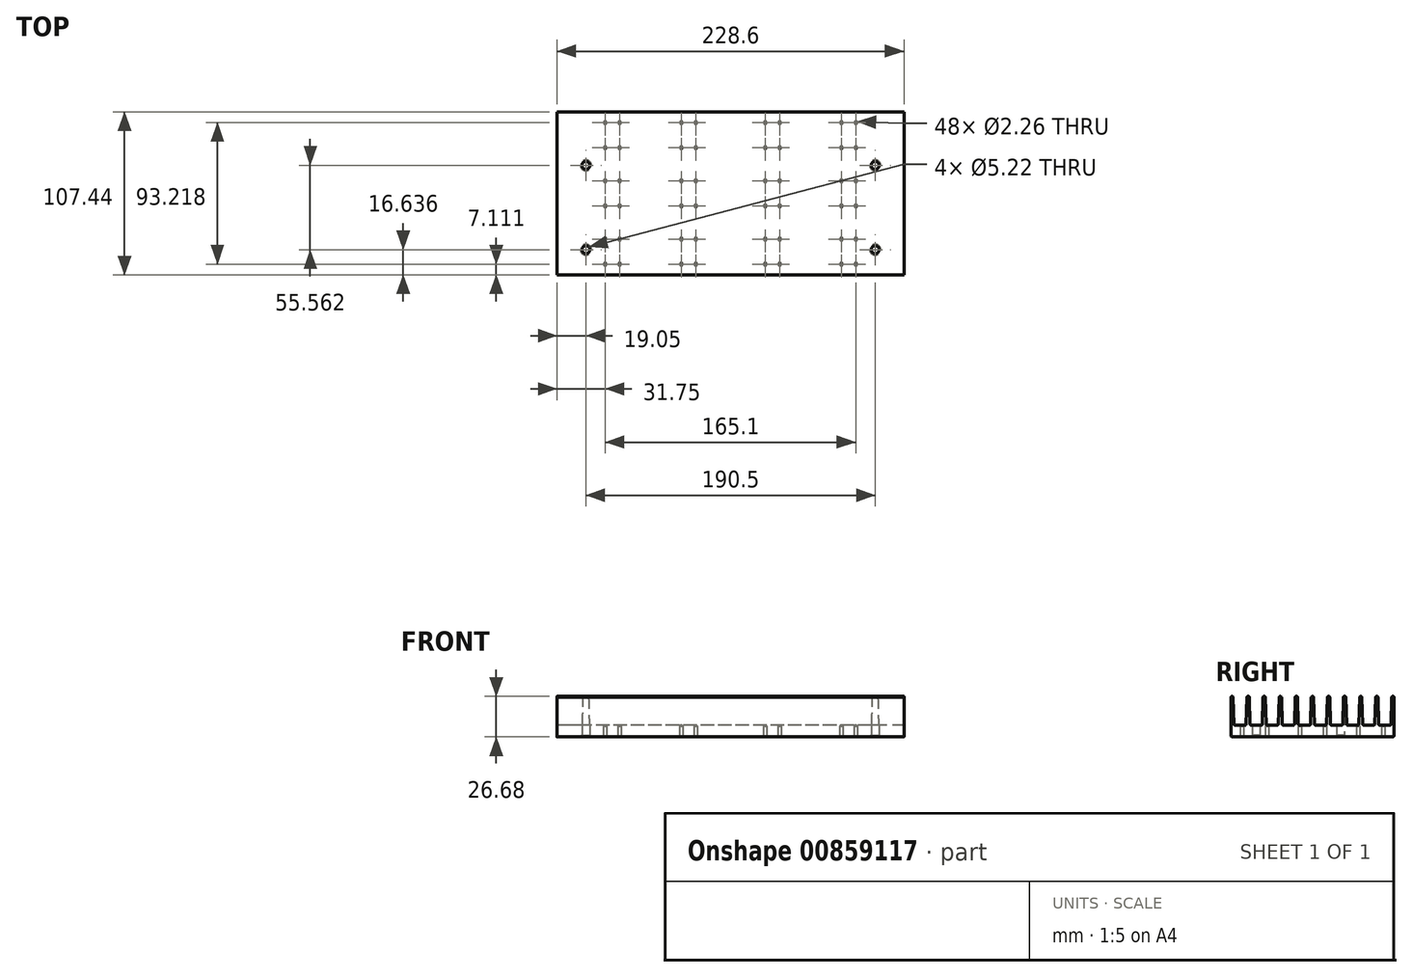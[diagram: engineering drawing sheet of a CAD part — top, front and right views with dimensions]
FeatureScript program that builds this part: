
annotation { "Feature Type Name" : "Feature", "Feature Type Description" : "" }
export const myFeature = defineFeature(function(context is Context, id is Id, definition is map)
    precondition{}
    {
        {
            var Q0;
            Q0=qCreatedBy(makeId("Right.planeOp"),FACE);
            var sketch = newSketch(context, id + "F0", { "sketchPlane" : qUnion([Q0])});
            skLineSegment(sketch, "E0", {"start": v(50.94, -5.71) * mm, "end": v(44.38, -5.71) * mm});
            skArc(sketch, "E1", {"start": v(43.62, -4.97) * mm, "mid": v(43.85, -5.5) * mm, "end": v(44.38, -5.71) * mm});
            skLineSegment(sketch, "E2", {"start": v(43.62, -4.97) * mm, "end": v(43.13, 12.59) * mm});
            skArc(sketch, "E3", {"start": v(43.13, 12.59) * mm, "mid": v(42.37, 13.33) * mm, "end": v(41.6, 12.59) * mm});
            skLineSegment(sketch, "E4", {"start": v(41.6, 12.59) * mm, "end": v(41.11, -4.97) * mm});
            skArc(sketch, "E5", {"start": v(40.35, -5.71) * mm, "mid": v(40.88, -5.5) * mm, "end": v(41.11, -4.97) * mm});
            skLineSegment(sketch, "E6", {"start": v(40.35, -5.71) * mm, "end": v(33.8, -5.71) * mm});
            skArc(sketch, "E7", {"start": v(33.03, -4.97) * mm, "mid": v(33.26, -5.5) * mm, "end": v(33.8, -5.71) * mm});
            skLineSegment(sketch, "E8", {"start": v(33.03, -4.97) * mm, "end": v(32.54, 12.59) * mm});
            skArc(sketch, "E9", {"start": v(32.54, 12.59) * mm, "mid": v(31.78, 13.33) * mm, "end": v(31.01, 12.59) * mm});
            skLineSegment(sketch, "E10", {"start": v(31.01, 12.59) * mm, "end": v(30.52, -4.97) * mm});
            skArc(sketch, "E11", {"start": v(29.76, -5.71) * mm, "mid": v(30.3, -5.5) * mm, "end": v(30.52, -4.97) * mm});
            skLineSegment(sketch, "E12", {"start": v(29.76, -5.71) * mm, "end": v(23.2, -5.71) * mm});
            skArc(sketch, "E13", {"start": v(22.44, -4.97) * mm, "mid": v(22.67, -5.5) * mm, "end": v(23.2, -5.71) * mm});
            skLineSegment(sketch, "E14", {"start": v(22.44, -4.97) * mm, "end": v(21.95, 12.59) * mm});
            skArc(sketch, "E15", {"start": v(21.95, 12.59) * mm, "mid": v(21.18, 13.33) * mm, "end": v(20.42, 12.59) * mm});
            skLineSegment(sketch, "E16", {"start": v(20.42, 12.59) * mm, "end": v(19.93, -4.97) * mm});
            skArc(sketch, "E17", {"start": v(19.17, -5.71) * mm, "mid": v(19.7, -5.5) * mm, "end": v(19.93, -4.97) * mm});
            skLineSegment(sketch, "E18", {"start": v(19.17, -5.71) * mm, "end": v(12.6, -5.71) * mm});
            skArc(sketch, "E19", {"start": v(11.85, -4.97) * mm, "mid": v(12.08, -5.5) * mm, "end": v(12.6, -5.71) * mm});
            skLineSegment(sketch, "E20", {"start": v(11.85, -4.97) * mm, "end": v(11.35, 12.59) * mm});
            skArc(sketch, "E21", {"start": v(11.35, 12.59) * mm, "mid": v(10.6, 13.33) * mm, "end": v(9.83, 12.59) * mm});
            skLineSegment(sketch, "E22", {"start": v(9.83, 12.59) * mm, "end": v(9.34, -4.97) * mm});
            skArc(sketch, "E23", {"start": v(8.58, -5.71) * mm, "mid": v(9.1, -5.5) * mm, "end": v(9.34, -4.97) * mm});
            skLineSegment(sketch, "E24", {"start": v(8.58, -5.71) * mm, "end": v(2.02, -5.71) * mm});
            skArc(sketch, "E25", {"start": v(1.25, -4.97) * mm, "mid": v(1.48, -5.5) * mm, "end": v(2.02, -5.71) * mm});
            skLineSegment(sketch, "E26", {"start": v(1.25, -4.97) * mm, "end": v(0.76, 12.59) * mm});
            skArc(sketch, "E27", {"start": v(0.76, 12.59) * mm, "mid": v(0, 13.33) * mm, "end": v(-0.76, 12.59) * mm});
            skLineSegment(sketch, "E28", {"start": v(-0.76, 12.59) * mm, "end": v(-1.25, -4.97) * mm});
            skArc(sketch, "E29", {"start": v(-2.02, -5.71) * mm, "mid": v(-1.48, -5.5) * mm, "end": v(-1.25, -4.97) * mm});
            skLineSegment(sketch, "E30", {"start": v(-2.02, -5.71) * mm, "end": v(-8.58, -5.71) * mm});
            skArc(sketch, "E31", {"start": v(-9.34, -4.97) * mm, "mid": v(-9.1, -5.5) * mm, "end": v(-8.58, -5.71) * mm});
            skLineSegment(sketch, "E32", {"start": v(-9.34, -4.97) * mm, "end": v(-9.83, 12.59) * mm});
            skArc(sketch, "E33", {"start": v(-9.83, 12.59) * mm, "mid": v(-10.6, 13.33) * mm, "end": v(-11.35, 12.59) * mm});
            skLineSegment(sketch, "E34", {"start": v(-11.35, 12.59) * mm, "end": v(-11.85, -4.97) * mm});
            skArc(sketch, "E35", {"start": v(-12.6, -5.71) * mm, "mid": v(-12.08, -5.5) * mm, "end": v(-11.85, -4.97) * mm});
            skLineSegment(sketch, "E36", {"start": v(-12.6, -5.71) * mm, "end": v(-19.17, -5.71) * mm});
            skArc(sketch, "E37", {"start": v(-19.93, -4.97) * mm, "mid": v(-19.7, -5.5) * mm, "end": v(-19.17, -5.71) * mm});
            skLineSegment(sketch, "E38", {"start": v(-19.93, -4.97) * mm, "end": v(-20.42, 12.59) * mm});
            skArc(sketch, "E39", {"start": v(-20.42, 12.59) * mm, "mid": v(-21.18, 13.34) * mm, "end": v(-21.95, 12.59) * mm});
            skLineSegment(sketch, "E40", {"start": v(-21.95, 12.59) * mm, "end": v(-22.44, -4.97) * mm});
            skArc(sketch, "E41", {"start": v(-23.2, -5.71) * mm, "mid": v(-22.67, -5.5) * mm, "end": v(-22.44, -4.97) * mm});
            skLineSegment(sketch, "E42", {"start": v(-23.2, -5.71) * mm, "end": v(-29.76, -5.71) * mm});
            skArc(sketch, "E43", {"start": v(-30.52, -4.97) * mm, "mid": v(-30.3, -5.5) * mm, "end": v(-29.76, -5.71) * mm});
            skLineSegment(sketch, "E44", {"start": v(-30.52, -4.97) * mm, "end": v(-31.01, 12.59) * mm});
            skArc(sketch, "E45", {"start": v(-31.01, 12.59) * mm, "mid": v(-31.78, 13.33) * mm, "end": v(-32.54, 12.59) * mm});
            skLineSegment(sketch, "E46", {"start": v(-32.54, 12.59) * mm, "end": v(-33.03, -4.97) * mm});
            skArc(sketch, "E47", {"start": v(-33.8, -5.71) * mm, "mid": v(-33.26, -5.5) * mm, "end": v(-33.03, -4.97) * mm});
            skLineSegment(sketch, "E48", {"start": v(-33.8, -5.71) * mm, "end": v(-40.35, -5.71) * mm});
            skArc(sketch, "E49", {"start": v(-41.11, -4.97) * mm, "mid": v(-40.88, -5.5) * mm, "end": v(-40.35, -5.71) * mm});
            skLineSegment(sketch, "E50", {"start": v(-41.11, -4.97) * mm, "end": v(-41.6, 12.59) * mm});
            skArc(sketch, "E51", {"start": v(-41.6, 12.59) * mm, "mid": v(-42.37, 13.33) * mm, "end": v(-43.13, 12.59) * mm});
            skLineSegment(sketch, "E52", {"start": v(-43.13, 12.59) * mm, "end": v(-43.62, -4.97) * mm});
            skArc(sketch, "E53", {"start": v(-44.38, -5.71) * mm, "mid": v(-43.85, -5.5) * mm, "end": v(-43.62, -4.97) * mm});
            skLineSegment(sketch, "E54", {"start": v(-44.38, -5.71) * mm, "end": v(-50.94, -5.71) * mm});
            skArc(sketch, "E55", {"start": v(-51.7, -4.97) * mm, "mid": v(-51.48, -5.5) * mm, "end": v(-50.94, -5.71) * mm});
            skLineSegment(sketch, "E56", {"start": v(-51.7, -4.97) * mm, "end": v(-52.2, 12.59) * mm});
            skArc(sketch, "E57", {"start": v(-52.2, 12.59) * mm, "mid": v(-52.96, 13.34) * mm, "end": v(-53.72, 12.59) * mm});
            skLineSegment(sketch, "E58", {"start": v(-53.72, 12.59) * mm, "end": v(-53.72, -12.57) * mm});
            skArc(sketch, "E59", {"start": v(-53.72, -12.57) * mm, "mid": v(-53.5, -13.11) * mm, "end": v(-52.96, -13.34) * mm});
            skLineSegment(sketch, "E60", {"start": v(-52.96, -13.33) * mm, "end": v(52.96, -13.33) * mm});
            skArc(sketch, "E61", {"start": v(52.96, -13.34) * mm, "mid": v(53.5, -13.11) * mm, "end": v(53.72, -12.57) * mm});
            skLineSegment(sketch, "E62", {"start": v(53.72, -12.57) * mm, "end": v(53.72, 12.59) * mm});
            skArc(sketch, "E63", {"start": v(53.72, 12.59) * mm, "mid": v(52.96, 13.33) * mm, "end": v(52.2, 12.59) * mm});
            skLineSegment(sketch, "E64", {"start": v(52.2, 12.59) * mm, "end": v(51.7, -4.97) * mm});
            skArc(sketch, "E65", {"start": v(50.94, -5.71) * mm, "mid": v(51.48, -5.5) * mm, "end": v(51.7, -4.97) * mm});
            skSolve(sketch);
        }
        {
            var Q0;
            Q0 = qSketchRegion(id + "F0", true);
            extrude(context, id + "F1", {"entities" : qUnion([Q0]), "endBound" : BoundingType.SYMMETRIC, "depth" : 228.6 * mm, "offsetDistance" : 25.4 * mm});
        }
        {
            var Q0;
            Q0=makeQuery(id+"F1.opExtrude","SWEPT_FACE",FACE,{"disambiguationData":[OSD([sQuery(id+"F0.wireOp",EDGE,"E60")])]});
            var sketch = newSketch(context, id + "F2", { "sketchPlane" : qUnion([Q0])});
            skLineSegment(sketch, "E66.0", {"start": v(-114.3, 52.96) * mm, "end": v(-114.3, -52.96) * mm});
            skLineSegment(sketch, "E67.0.2", {"start": v(114.3, -52.96) * mm, "end": v(114.3, 52.96) * mm});
            skPoint(sketch, "E68", {"position": v(-95.25, 37.08) * mm});
            skPoint(sketch, "E69", {"position": v(95.25, 37.08) * mm});
            skPoint(sketch, "E70", {"position": v(14.56, 92.82) * mm});
            skPoint(sketch, "E71", {"position": v(-95.25, -18.48) * mm});
            skPoint(sketch, "E72", {"position": v(95.25, -18.48) * mm});
            skSolve(sketch);
        }
        {
            var Q0;
            Q0=sQuery(id+"F2.wireOp",VERTEX,"E68");
            var Q1;
            Q1=sQuery(id+"F2.wireOp",VERTEX,"E71");
            var Q2;
            Q2=sQuery(id+"F2.wireOp",VERTEX,"E69");
            var Q3;
            Q3=sQuery(id+"F2.wireOp",VERTEX,"E72");
            var Q4;
            Q4=makeQuery(id+"F1.opExtrude","SWEPT_BODY",BODY,{"disambiguationData":[OSD([sQuery(id+"F0.wireOp",EDGE,"E0"),sQuery(id+"F0.wireOp",EDGE,"E1"),sQuery(id+"F0.wireOp",EDGE,"E2"),sQuery(id+"F0.wireOp",EDGE,"E3"),sQuery(id+"F0.wireOp",EDGE,"E4"),sQuery(id+"F0.wireOp",EDGE,"E5"),sQuery(id+"F0.wireOp",EDGE,"E6"),sQuery(id+"F0.wireOp",EDGE,"E7"),sQuery(id+"F0.wireOp",EDGE,"E8"),sQuery(id+"F0.wireOp",EDGE,"E9"),sQuery(id+"F0.wireOp",EDGE,"E10"),sQuery(id+"F0.wireOp",EDGE,"E11"),sQuery(id+"F0.wireOp",EDGE,"E12"),sQuery(id+"F0.wireOp",EDGE,"E13"),sQuery(id+"F0.wireOp",EDGE,"E14"),sQuery(id+"F0.wireOp",EDGE,"E15"),sQuery(id+"F0.wireOp",EDGE,"E16"),sQuery(id+"F0.wireOp",EDGE,"E17"),sQuery(id+"F0.wireOp",EDGE,"E18"),sQuery(id+"F0.wireOp",EDGE,"E19"),sQuery(id+"F0.wireOp",EDGE,"E20"),sQuery(id+"F0.wireOp",EDGE,"E21"),sQuery(id+"F0.wireOp",EDGE,"E22"),sQuery(id+"F0.wireOp",EDGE,"E23"),sQuery(id+"F0.wireOp",EDGE,"E24"),sQuery(id+"F0.wireOp",EDGE,"E25"),sQuery(id+"F0.wireOp",EDGE,"E26"),sQuery(id+"F0.wireOp",EDGE,"E27"),sQuery(id+"F0.wireOp",EDGE,"E28"),sQuery(id+"F0.wireOp",EDGE,"E29"),sQuery(id+"F0.wireOp",EDGE,"E30"),sQuery(id+"F0.wireOp",EDGE,"E31"),sQuery(id+"F0.wireOp",EDGE,"E32"),sQuery(id+"F0.wireOp",EDGE,"E33"),sQuery(id+"F0.wireOp",EDGE,"E34"),sQuery(id+"F0.wireOp",EDGE,"E35"),sQuery(id+"F0.wireOp",EDGE,"E36"),sQuery(id+"F0.wireOp",EDGE,"E37"),sQuery(id+"F0.wireOp",EDGE,"E38"),sQuery(id+"F0.wireOp",EDGE,"E39"),sQuery(id+"F0.wireOp",EDGE,"E40"),sQuery(id+"F0.wireOp",EDGE,"E41"),sQuery(id+"F0.wireOp",EDGE,"E42"),sQuery(id+"F0.wireOp",EDGE,"E43"),sQuery(id+"F0.wireOp",EDGE,"E44"),sQuery(id+"F0.wireOp",EDGE,"E45"),sQuery(id+"F0.wireOp",EDGE,"E46"),sQuery(id+"F0.wireOp",EDGE,"E47"),sQuery(id+"F0.wireOp",EDGE,"E48"),sQuery(id+"F0.wireOp",EDGE,"E49"),sQuery(id+"F0.wireOp",EDGE,"E50"),sQuery(id+"F0.wireOp",EDGE,"E51"),sQuery(id+"F0.wireOp",EDGE,"E52"),sQuery(id+"F0.wireOp",EDGE,"E53"),sQuery(id+"F0.wireOp",EDGE,"E54"),sQuery(id+"F0.wireOp",EDGE,"E55"),sQuery(id+"F0.wireOp",EDGE,"E56"),sQuery(id+"F0.wireOp",EDGE,"E57"),sQuery(id+"F0.wireOp",EDGE,"E58"),sQuery(id+"F0.wireOp",EDGE,"E59"),sQuery(id+"F0.wireOp",EDGE,"E60"),sQuery(id+"F0.wireOp",EDGE,"E61"),sQuery(id+"F0.wireOp",EDGE,"E62"),sQuery(id+"F0.wireOp",EDGE,"E63"),sQuery(id+"F0.wireOp",EDGE,"E64"),sQuery(id+"F0.wireOp",EDGE,"E65")])]});
            hole(context, id + "F3", {"style" : HoleStyle.C_SINK, "endStyle" : HoleEndStyle.THROUGH, "standardTappedOrClearance" : lookupTablePath({ "standard" : "ANSI", "size" : "#5 (0.2)", "type" : "Drilled" }), "standardBlindInLast" : lookupTablePath({ "standard" : "ANSI", "size" : "#5", "type" : "Drilled" }), "holeDiameter" : 5.22 * mm, "cSinkDiameter" : 7.14 * mm, "cSinkAngle" : 82 * degree, "majorDiameter" : 2.84 * mm, "isTappedThrough" : true, "tappedDepth" : 5.2 * mm, "tapClearance" : 3, "locations" : qUnion([Q0, Q1, Q2, Q3]), "scope" : qUnion([Q4])});
        }
        {
            var Q0;
            Q0=makeQuery(id+"F1.opExtrude","SWEPT_FACE",FACE,{"disambiguationData":[OSD([sQuery(id+"F0.wireOp",EDGE,"E60")])]});
            var sketch = newSketch(context, id + "F4", { "sketchPlane" : qUnion([Q0])});
            skPoint(sketch, "E73", {"position": v(-82.55, 46.6) * mm});
            skPoint(sketch, "E74", {"position": v(-73.03, 46.6) * mm});
            skPoint(sketch, "E75", {"position": v(-82.55, 30.1) * mm});
            skPoint(sketch, "E76", {"position": v(-73.02, 30.1) * mm});
            skPoint(sketch, "E77", {"position": v(-32.38, 46.6) * mm});
            skPoint(sketch, "E78", {"position": v(-22.86, 46.6) * mm});
            skPoint(sketch, "E79", {"position": v(-32.39, 30.1) * mm});
            skPoint(sketch, "E80", {"position": v(-22.86, 30.1) * mm});
            skPoint(sketch, "E81.MirrorP", {"position": v(82.55, 46.6) * mm});
            skPoint(sketch, "E82.MirrorP", {"position": v(73.03, 46.6) * mm});
            skPoint(sketch, "E83.MirrorP", {"position": v(82.55, 30.1) * mm});
            skPoint(sketch, "E84.MirrorP", {"position": v(73.02, 30.1) * mm});
            skPoint(sketch, "E85.MirrorP", {"position": v(32.38, 46.6) * mm});
            skPoint(sketch, "E86.MirrorP", {"position": v(22.86, 46.6) * mm});
            skPoint(sketch, "E87.MirrorP", {"position": v(22.86, 30.1) * mm});
            skPoint(sketch, "E88.MirrorP", {"position": v(32.39, 30.1) * mm});
            skPoint(sketch, "E89.MirrorP", {"position": v(-82.55, -46.6) * mm});
            skPoint(sketch, "E90.MirrorP", {"position": v(-73.03, -46.6) * mm});
            skPoint(sketch, "E91.MirrorP", {"position": v(-73.02, -30.1) * mm});
            skPoint(sketch, "E92.MirrorP", {"position": v(-82.55, -30.1) * mm});
            skPoint(sketch, "E93.MirrorP", {"position": v(-32.38, -46.6) * mm});
            skPoint(sketch, "E94.MirrorP", {"position": v(-22.86, -46.6) * mm});
            skPoint(sketch, "E95.MirrorP", {"position": v(-22.86, -30.1) * mm});
            skPoint(sketch, "E96.MirrorP", {"position": v(-32.39, -30.1) * mm});
            skPoint(sketch, "E97.MirrorP", {"position": v(22.86, -46.6) * mm});
            skPoint(sketch, "E98.MirrorP", {"position": v(32.38, -46.6) * mm});
            skPoint(sketch, "E99.MirrorP", {"position": v(22.86, -30.1) * mm});
            skPoint(sketch, "E100.MirrorP", {"position": v(32.39, -30.1) * mm});
            skPoint(sketch, "E101.MirrorP", {"position": v(73.03, -46.6) * mm});
            skPoint(sketch, "E102.MirrorP", {"position": v(82.55, -46.6) * mm});
            skPoint(sketch, "E103.MirrorP", {"position": v(82.55, -30.1) * mm});
            skPoint(sketch, "E104.MirrorP", {"position": v(73.02, -30.1) * mm});
            skPoint(sketch, "E105", {"position": v(-82.55, 8.25) * mm});
            skPoint(sketch, "E106", {"position": v(-82.55, -8.26) * mm});
            skPoint(sketch, "E107", {"position": v(-73.03, 8.25) * mm});
            skPoint(sketch, "E108", {"position": v(-73.02, -8.26) * mm});
            skPoint(sketch, "E109", {"position": v(-32.38, 8.25) * mm});
            skPoint(sketch, "E110", {"position": v(-22.86, 8.25) * mm});
            skPoint(sketch, "E111", {"position": v(-32.38, -8.26) * mm});
            skPoint(sketch, "E112", {"position": v(-22.86, -8.26) * mm});
            skPoint(sketch, "E113.MirrorP", {"position": v(82.55, 8.25) * mm});
            skPoint(sketch, "E114.MirrorP", {"position": v(73.03, 8.25) * mm});
            skPoint(sketch, "E115.MirrorP", {"position": v(32.38, 8.25) * mm});
            skPoint(sketch, "E116.MirrorP", {"position": v(22.86, 8.25) * mm});
            skPoint(sketch, "E117.MirrorP", {"position": v(22.86, -8.26) * mm});
            skPoint(sketch, "E118.MirrorP", {"position": v(32.38, -8.26) * mm});
            skPoint(sketch, "E119.MirrorP", {"position": v(73.02, -8.26) * mm});
            skPoint(sketch, "E120.MirrorP", {"position": v(82.55, -8.26) * mm});
            skSolve(sketch);
        }
        {
            var Q0;
            Q0=sQuery(id+"F4.wireOp",VERTEX,"E73");
            var Q1;
            Q1=sQuery(id+"F4.wireOp",VERTEX,"E74");
            var Q2;
            Q2=sQuery(id+"F4.wireOp",VERTEX,"E76");
            var Q3;
            Q3=sQuery(id+"F4.wireOp",VERTEX,"E75");
            var Q4;
            Q4=sQuery(id+"F4.wireOp",VERTEX,"E105");
            var Q5;
            Q5=sQuery(id+"F4.wireOp",VERTEX,"E107");
            var Q6;
            Q6=sQuery(id+"F4.wireOp",VERTEX,"E108");
            var Q7;
            Q7=sQuery(id+"F4.wireOp",VERTEX,"E106");
            var Q8;
            Q8=sQuery(id+"F4.wireOp",VERTEX,"E92.MirrorP");
            var Q9;
            Q9=sQuery(id+"F4.wireOp",VERTEX,"E91.MirrorP");
            var Q10;
            Q10=sQuery(id+"F4.wireOp",VERTEX,"E90.MirrorP");
            var Q11;
            Q11=sQuery(id+"F4.wireOp",VERTEX,"E89.MirrorP");
            var Q12;
            Q12=sQuery(id+"F4.wireOp",VERTEX,"E77");
            var Q13;
            Q13=sQuery(id+"F4.wireOp",VERTEX,"E78");
            var Q14;
            Q14=sQuery(id+"F4.wireOp",VERTEX,"E80");
            var Q15;
            Q15=sQuery(id+"F4.wireOp",VERTEX,"E79");
            var Q16;
            Q16=sQuery(id+"F4.wireOp",VERTEX,"E109");
            var Q17;
            Q17=sQuery(id+"F4.wireOp",VERTEX,"E110");
            var Q18;
            Q18=sQuery(id+"F4.wireOp",VERTEX,"E112");
            var Q19;
            Q19=sQuery(id+"F4.wireOp",VERTEX,"E111");
            var Q20;
            Q20=sQuery(id+"F4.wireOp",VERTEX,"E96.MirrorP");
            var Q21;
            Q21=sQuery(id+"F4.wireOp",VERTEX,"E95.MirrorP");
            var Q22;
            Q22=sQuery(id+"F4.wireOp",VERTEX,"E94.MirrorP");
            var Q23;
            Q23=sQuery(id+"F4.wireOp",VERTEX,"E93.MirrorP");
            var Q24;
            Q24=sQuery(id+"F4.wireOp",VERTEX,"E86.MirrorP");
            var Q25;
            Q25=sQuery(id+"F4.wireOp",VERTEX,"E85.MirrorP");
            var Q26;
            Q26=sQuery(id+"F4.wireOp",VERTEX,"E87.MirrorP");
            var Q27;
            Q27=sQuery(id+"F4.wireOp",VERTEX,"E88.MirrorP");
            var Q28;
            Q28=sQuery(id+"F4.wireOp",VERTEX,"E116.MirrorP");
            var Q29;
            Q29=sQuery(id+"F4.wireOp",VERTEX,"E115.MirrorP");
            var Q30;
            Q30=sQuery(id+"F4.wireOp",VERTEX,"E117.MirrorP");
            var Q31;
            Q31=sQuery(id+"F4.wireOp",VERTEX,"E118.MirrorP");
            var Q32;
            Q32=sQuery(id+"F4.wireOp",VERTEX,"E99.MirrorP");
            var Q33;
            Q33=sQuery(id+"F4.wireOp",VERTEX,"E100.MirrorP");
            var Q34;
            Q34=sQuery(id+"F4.wireOp",VERTEX,"E97.MirrorP");
            var Q35;
            Q35=sQuery(id+"F4.wireOp",VERTEX,"E98.MirrorP");
            var Q36;
            Q36=sQuery(id+"F4.wireOp",VERTEX,"E82.MirrorP");
            var Q37;
            Q37=sQuery(id+"F4.wireOp",VERTEX,"E81.MirrorP");
            var Q38;
            Q38=sQuery(id+"F4.wireOp",VERTEX,"E84.MirrorP");
            var Q39;
            Q39=sQuery(id+"F4.wireOp",VERTEX,"E83.MirrorP");
            var Q40;
            Q40=sQuery(id+"F4.wireOp",VERTEX,"E114.MirrorP");
            var Q41;
            Q41=sQuery(id+"F4.wireOp",VERTEX,"E113.MirrorP");
            var Q42;
            Q42=sQuery(id+"F4.wireOp",VERTEX,"E119.MirrorP");
            var Q43;
            Q43=sQuery(id+"F4.wireOp",VERTEX,"E120.MirrorP");
            var Q44;
            Q44=sQuery(id+"F4.wireOp",VERTEX,"E104.MirrorP");
            var Q45;
            Q45=sQuery(id+"F4.wireOp",VERTEX,"E103.MirrorP");
            var Q46;
            Q46=sQuery(id+"F4.wireOp",VERTEX,"E102.MirrorP");
            var Q47;
            Q47=sQuery(id+"F4.wireOp",VERTEX,"E101.MirrorP");
            var Q48;
            Q48=makeQuery(id+"F1.opExtrude","SWEPT_BODY",BODY,{"disambiguationData":[OSD([sQuery(id+"F0.wireOp",EDGE,"E0"),sQuery(id+"F0.wireOp",EDGE,"E1"),sQuery(id+"F0.wireOp",EDGE,"E2"),sQuery(id+"F0.wireOp",EDGE,"E3"),sQuery(id+"F0.wireOp",EDGE,"E4"),sQuery(id+"F0.wireOp",EDGE,"E5"),sQuery(id+"F0.wireOp",EDGE,"E6"),sQuery(id+"F0.wireOp",EDGE,"E7"),sQuery(id+"F0.wireOp",EDGE,"E8"),sQuery(id+"F0.wireOp",EDGE,"E9"),sQuery(id+"F0.wireOp",EDGE,"E10"),sQuery(id+"F0.wireOp",EDGE,"E11"),sQuery(id+"F0.wireOp",EDGE,"E12"),sQuery(id+"F0.wireOp",EDGE,"E13"),sQuery(id+"F0.wireOp",EDGE,"E14"),sQuery(id+"F0.wireOp",EDGE,"E15"),sQuery(id+"F0.wireOp",EDGE,"E16"),sQuery(id+"F0.wireOp",EDGE,"E17"),sQuery(id+"F0.wireOp",EDGE,"E18"),sQuery(id+"F0.wireOp",EDGE,"E19"),sQuery(id+"F0.wireOp",EDGE,"E20"),sQuery(id+"F0.wireOp",EDGE,"E21"),sQuery(id+"F0.wireOp",EDGE,"E22"),sQuery(id+"F0.wireOp",EDGE,"E23"),sQuery(id+"F0.wireOp",EDGE,"E24"),sQuery(id+"F0.wireOp",EDGE,"E25"),sQuery(id+"F0.wireOp",EDGE,"E26"),sQuery(id+"F0.wireOp",EDGE,"E27"),sQuery(id+"F0.wireOp",EDGE,"E28"),sQuery(id+"F0.wireOp",EDGE,"E29"),sQuery(id+"F0.wireOp",EDGE,"E30"),sQuery(id+"F0.wireOp",EDGE,"E31"),sQuery(id+"F0.wireOp",EDGE,"E32"),sQuery(id+"F0.wireOp",EDGE,"E33"),sQuery(id+"F0.wireOp",EDGE,"E34"),sQuery(id+"F0.wireOp",EDGE,"E35"),sQuery(id+"F0.wireOp",EDGE,"E36"),sQuery(id+"F0.wireOp",EDGE,"E37"),sQuery(id+"F0.wireOp",EDGE,"E38"),sQuery(id+"F0.wireOp",EDGE,"E39"),sQuery(id+"F0.wireOp",EDGE,"E40"),sQuery(id+"F0.wireOp",EDGE,"E41"),sQuery(id+"F0.wireOp",EDGE,"E42"),sQuery(id+"F0.wireOp",EDGE,"E43"),sQuery(id+"F0.wireOp",EDGE,"E44"),sQuery(id+"F0.wireOp",EDGE,"E45"),sQuery(id+"F0.wireOp",EDGE,"E46"),sQuery(id+"F0.wireOp",EDGE,"E47"),sQuery(id+"F0.wireOp",EDGE,"E48"),sQuery(id+"F0.wireOp",EDGE,"E49"),sQuery(id+"F0.wireOp",EDGE,"E50"),sQuery(id+"F0.wireOp",EDGE,"E51"),sQuery(id+"F0.wireOp",EDGE,"E52"),sQuery(id+"F0.wireOp",EDGE,"E53"),sQuery(id+"F0.wireOp",EDGE,"E54"),sQuery(id+"F0.wireOp",EDGE,"E55"),sQuery(id+"F0.wireOp",EDGE,"E56"),sQuery(id+"F0.wireOp",EDGE,"E57"),sQuery(id+"F0.wireOp",EDGE,"E58"),sQuery(id+"F0.wireOp",EDGE,"E59"),sQuery(id+"F0.wireOp",EDGE,"E60"),sQuery(id+"F0.wireOp",EDGE,"E61"),sQuery(id+"F0.wireOp",EDGE,"E62"),sQuery(id+"F0.wireOp",EDGE,"E63"),sQuery(id+"F0.wireOp",EDGE,"E64"),sQuery(id+"F0.wireOp",EDGE,"E65")])]});
            hole(context, id + "F5", {"style" : HoleStyle.SIMPLE, "endStyle" : HoleEndStyle.BLIND, "standardTappedOrClearance" : lookupTablePath({ "standard" : "ANSI", "engagement" : "75%", "pitch" : "40 tpi", "size" : "#4", "type" : "Tapped" }), "standardBlindInLast" : lookupTablePath({ "standard" : "ANSI", "engagement" : "75%", "pitch" : "40 tpi", "size" : "#4", "type" : "Tapped" }), "holeDiameter" : 2.26 * mm, "majorDiameter" : 2.84 * mm, "showTappedDepth" : true, "holeDepth" : 7.11 * mm, "isTappedThrough" : true, "tappedDepth" : 5.2 * mm, "tapClearance" : 3, "locations" : qUnion([Q0, Q1, Q2, Q3, Q4, Q5, Q6, Q7, Q8, Q9, Q10, Q11, Q12, Q13, Q14, Q15, Q16, Q17, Q18, Q19, Q20, Q21, Q22, Q23, Q24, Q25, Q26, Q27, Q28, Q29, Q30, Q31, Q32, Q33, Q34, Q35, Q36, Q37, Q38, Q39, Q40, Q41, Q42, Q43, Q44, Q45, Q46, Q47]), "scope" : qUnion([Q48])});
        }
    });
